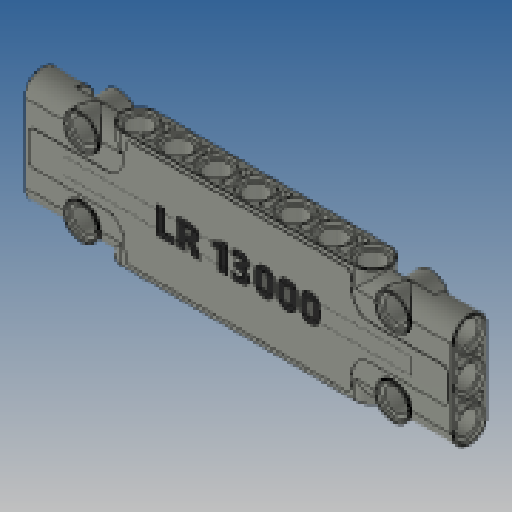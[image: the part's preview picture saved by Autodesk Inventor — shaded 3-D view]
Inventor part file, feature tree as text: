
AUTODESK INVENTOR PART (.ipt)
format: ipt  version: 2025 (Build 290162010, 162A)  size: 1,303,552 bytes
history: native  units: in
note: dims shown in document units (in); Inventor stores cm internally (conversion verified against a paired STEP export)
features: extrude x18, sketch x13, mirror x5, plane x1, fillet x1
ambient origin geometry x8: Origin, YZ Plane, XZ Plane, XY Plane, X Axis, Y Axis, Z Axis, Center Point
bodies: Solid1 (feature_tree)
feature tree (38):
  extrude  "Extrusion1"  Depth=0.189in
  sketch  "Sketch3"  dims[d6=0.189in d7=0.252in]
  extrude  "Extrusion2"  Depth=0.0315in
  extrude  "Extrusion3"  TaperAngle=0.0deg  [1 undecoded]
  extrude  "Extrusion4"  Depth=0.252in
  plane  "Work Plane1"
  extrude  "Extrusion5"  Depth=0.7874in
  sketch  "Sketch5"  dims[d12=0.3937in d14=0.3937in d16=0.2835in]
  extrude  "Extrusion6"  Depth=0.2835in
  extrude  "Extrusion7"  Depth=0.0315in
  extrude  "Extrusion10"  Depth=0.2205in TaperAngle=0.0deg
  extrude  "Extrusion8"  Depth=0.189in
  extrude  "Extrusion9"  Depth=0.0315in TaperAngle=0.0deg
  mirror  "Mirror1"
  mirror  "Mirror2"
  sketch  "Sketch8"  dims[d22=-0.1417in d23=0.189in]
  extrude  "Extrusion11"  Depth=0.189in
  extrude  "Extrusion12"  Depth=0.2677in
  extrude  "Extrusion13"  Depth=0.2677in TaperAngle=0.0deg
  sketch  "Sketch9"  dims[d24=0.2835in d25=0.0315in d26=0.0in]
  extrude  "Extrusion14"  Depth=0.252in
  extrude  "Extrusion16"  Depth=0.0315in
  mirror  "Mirror3"
  extrude  "Extrusion15"  TaperAngle=0.0deg  [1 undecoded]
  fillet  "Fillet1"  Radius=0.252in
  extrude  "Extrusion17"  Depth=0.0315in
  mirror  "Spiegeln4"
  mirror  "Spiegeln5"
  extrude  "Extrusion18"  TaperAngle=0.0deg  [1 undecoded]
  sketch  "Sketch2"  dims[d2=0.2835in d3=0.0315in]
  sketch  "Skizze - Rechteckige Anordnung1"  dims[d0=0.315in d1=0.189in]
  sketch  "Sketch4"  dims[d8=45.0deg d9=0.7874in d11=0.315in]
  sketch  "Sketch6"  dims[d17=0.0in d18=0.0315in]
  sketch  "Sketch7"  dims[d19=0.0in d20=0.2205in d21=0.0in]
  sketch  "Sketch10"  dims[d27=0.2835in d28=0.189in]
  sketch  "Skizze - Rechteckige Anordnung2"  dims[d4=3.4646in d5=0.0in]
  sketch  "Skizze11"  dims[d29=1.2598in d30=0.2677in d31=0.0472in]
  sketch  "Skizze12"  dims[d32=0.0in d33=0.0in d34=0.2677in d35=0.0in d36=0.252in d37=0.0315in d38=0.0in d39=0.252in d40=0.0315in d41=0.0in d42=0.0315in d43=0.2205in d44=0.0in d45=0.2835in d46=1.8898in d47=0.189in d48=0.1417in d49=0.1417in d50=0.0in d51=0.0in d52=0.1417in d53=0.0in d54=0.315in d55=0.0in d56=0.252in d57=0.0315in d58=0.0in d59=2.8031in d60=0.126in d62=0.0079in d63=0.0in d64=45.0deg d65=2.3622in d67=0.315in d68=0.3937in d70=0.3937in d72=0.2205in d73=0.0in d74=0.0039in d75=0.0157in d76=0.6528in d77=0.0394in d78=0.1378in d79=0.0394in d80=0.0394in d81=0.0394in d82=0.8268in d83=0.1575in d84=0.0039in d85=0.0in d86=0.0004in d87=0.0in]
note: 3 required parameter values undecoded (feature->parameter linkage not recoverable at this tier; creation-order binding heuristic only, values carry confidence <= 0.55)
